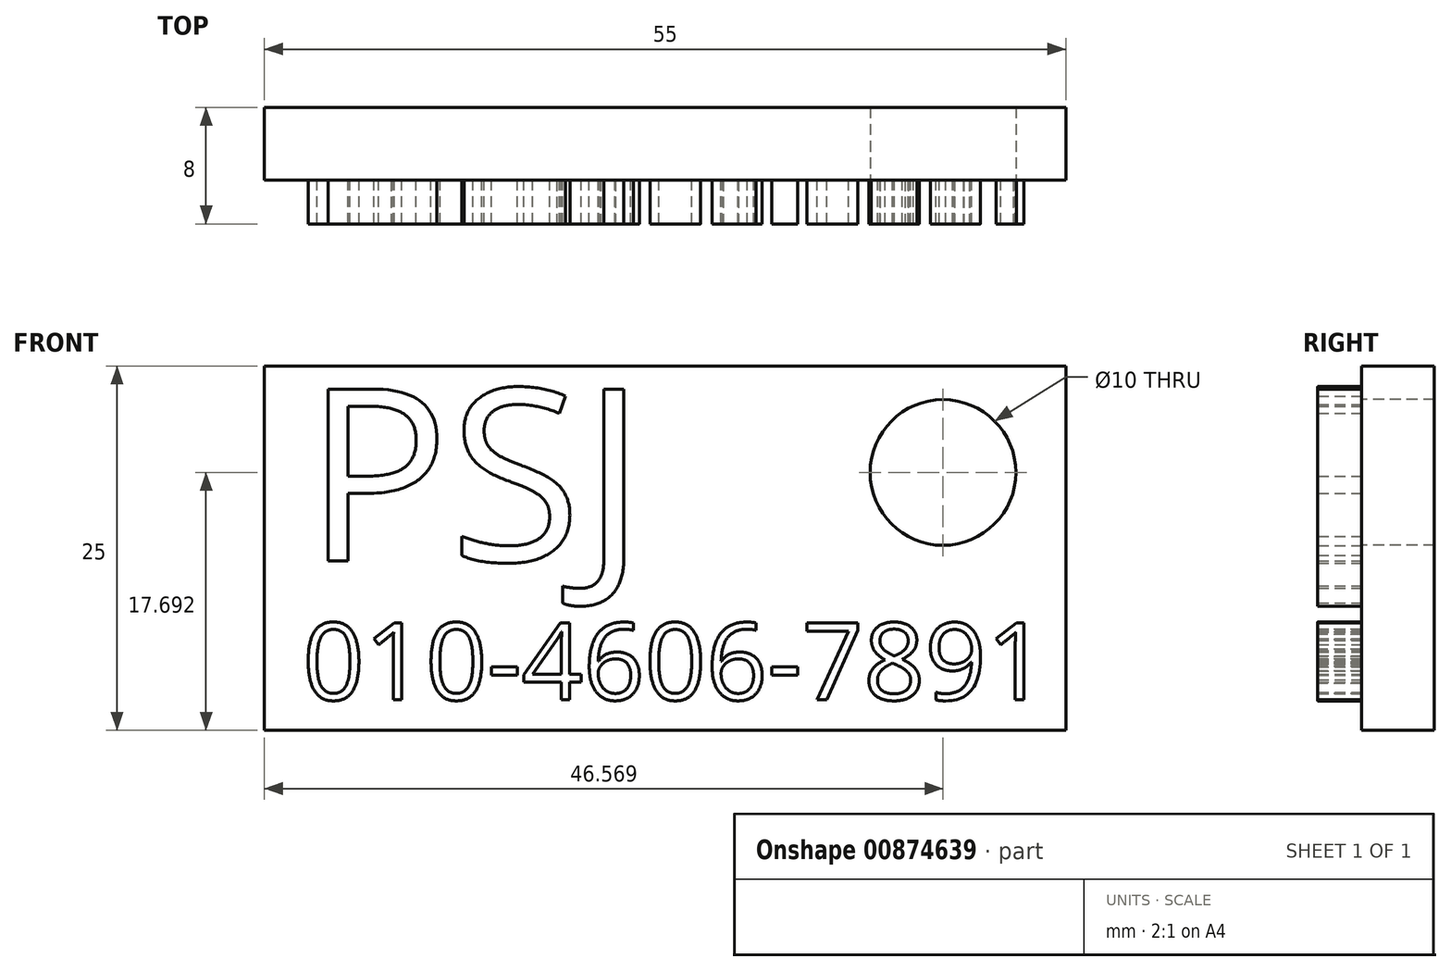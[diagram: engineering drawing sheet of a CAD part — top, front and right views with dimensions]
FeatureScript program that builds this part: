
annotation { "Feature Type Name" : "Feature", "Feature Type Description" : "" }
export const myFeature = defineFeature(function(context is Context, id is Id, definition is map)
    precondition{}
    {
        {
            var Q0;
            Q0=qCreatedBy(makeId("Front.planeOp"),FACE);
            var sketch = newSketch(context, id + "F0", { "sketchPlane" : qUnion([Q0])});
            skLineSegment(sketch, "E0.bottom", {"start": v(0, 0) * mm, "end": v(55, 0) * mm});
            skLineSegment(sketch, "E0.top", {"start": v(0, 25) * mm, "end": v(55, 25) * mm});
            skLineSegment(sketch, "E0.left", {"start": v(0, 0) * mm, "end": v(0, 25) * mm});
            skLineSegment(sketch, "E0.right", {"start": v(55, 0) * mm, "end": v(55, 25) * mm});
            skSolve(sketch);
        }
        {
            var Q0;
            Q0=makeQuery(id+"F0.imprint","IMPRINT",FACE,{"disambiguationData":[TD([[makeQuery(id+"F0.imprint","IMPRINT",EDGE,{"derivedFrom":sQuery(id+"F0.wireOp",EDGE,"E0.bottom")}),1.0]])]});
            extrude(context, id + "F1", {"entities" : qUnion([Q0]), "depth" : 5 * mm, "offsetDistance" : 25 * mm});
        }
        {
            var Q0;
            Q0=makeQuery(id+"F1.opExtrude","CAP_FACE",FACE,{"disambiguationData":[OSD([sQuery(id+"F0.wireOp",EDGE,"E0.bottom"),sQuery(id+"F0.wireOp",EDGE,"E0.top"),sQuery(id+"F0.wireOp",EDGE,"E0.left"),sQuery(id+"F0.wireOp",EDGE,"E0.right")])],"isStart":false});
            var sketch = newSketch(context, id + "F2", { "sketchPlane" : qUnion([Q0])});
            skText(sketch, "E1", { "text": "PSJ\n", "fontName": "OpenSans-Regular.ttf"});
            skText(sketch, "E2", { "text": "010-4606-7891\n", "fontName": "OpenSans-Regular.ttf"});
            const initialGuessF2  = {"E1": [0.00273, 0.01162, 1, 0, 0.0119], "E2": [0.00263, 0.00209, 1, 0, 0.00531]};
            skSetInitialGuess(sketch, initialGuessF2);
            skSolve(sketch);
        }
        {
            var Q0;
            Q0=qSketchRegion(id+"F2",true);
            extrude(context, id + "F3", {"entities" : qUnion([Q0]), "operationType" : NewBodyOperationType.ADD, "depth" : 3 * mm, "offsetDistance" : 25 * mm});
        }
        {
            var Q0;
            {var subQ0=sQuery(id+"F0.wireOp",EDGE,"E0.top");var subQ1=sQuery(id+"F0.wireOp",EDGE,"E0.right");var subQ2=sQuery(id+"F0.wireOp",EDGE,"E0.bottom");var subQ3=sQuery(id+"F0.wireOp",EDGE,"E0.left");Q0=makeQuery(id+"F3.boolean.opBoolean","SPLIT",FACE,{"disambiguationData":[TD([makeQuery(id+"F1.opExtrude","SWEPT_FACE",FACE,{"disambiguationData":[OSD([subQ2])]})])],"derivedFrom":makeQuery(id+"F1.opExtrude","CAP_FACE",FACE,{"disambiguationData":[OSD([subQ2,subQ0,subQ3,subQ1])],"isStart":false})});}
            var sketch = newSketch(context, id + "F4", { "sketchPlane" : qUnion([Q0])});
            skCircle(sketch, "E3", {"center": v(46.57, 17.7) * mm, "radius": 5 * mm});
            skSolve(sketch);
        }
        {
            var Q0;
            Q0=makeQuery(id+"F4.imprint","IMPRINT",FACE,{"disambiguationData":[TD([[makeQuery(id+"F4.imprint","IMPRINT",EDGE,{"derivedFrom":sQuery(id+"F4.wireOp",EDGE,"E3")}),1.0]])]});
            extrude(context, id + "F5", {"entities" : qUnion([Q0]), "operationType" : NewBodyOperationType.REMOVE, "endBound" : BoundingType.THROUGH_ALL, "oppositeDirection" : true, "depth" : 25 * mm, "offsetDistance" : 25 * mm});
        }
    });
